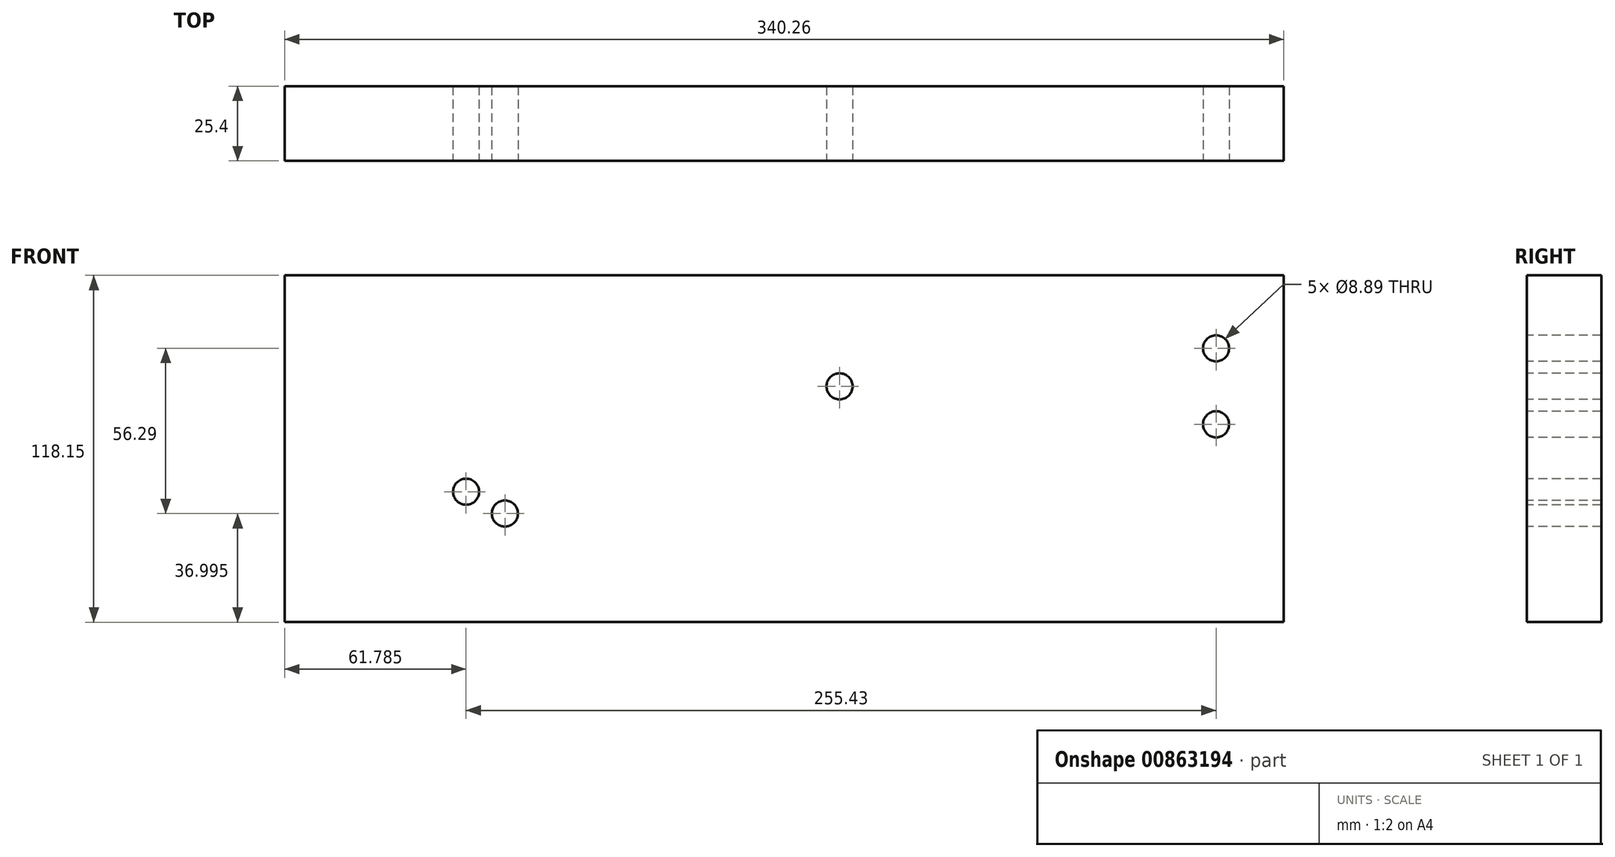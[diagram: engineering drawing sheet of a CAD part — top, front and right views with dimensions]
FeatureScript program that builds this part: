
annotation { "Feature Type Name" : "Feature", "Feature Type Description" : "" }
export const myFeature = defineFeature(function(context is Context, id is Id, definition is map)
    precondition{}
    {
        {
            var Q0;
            Q0=qCreatedBy(makeId("Front.planeOp"),FACE);
            var sketch = newSketch(context, id + "F0", { "sketchPlane" : qUnion([Q0])});
            skLineSegment(sketch, "E0.bottom", {"start": v(-97.64, 50.75) * mm, "end": v(242.62, 50.75) * mm});
            skLineSegment(sketch, "E0.top", {"start": v(-97.64, -67.4) * mm, "end": v(242.62, -67.4) * mm});
            skLineSegment(sketch, "E0.left", {"start": v(-97.64, 50.75) * mm, "end": v(-97.64, -67.4) * mm});
            skLineSegment(sketch, "E0.right", {"start": v(242.62, 50.75) * mm, "end": v(242.62, -67.4) * mm});
            skSolve(sketch);
        }
        {
            var Q0;
            Q0 = qSketchRegion(id + "F0", true);
            extrude(context, id + "F1", {"entities" : qUnion([Q0]), "depth" : 25.4 * mm, "offsetDistance" : 25.4 * mm});
        }
        {
            var Q0;
            Q0=makeQuery(id+"F1.opExtrude","CAP_FACE",FACE,{"disambiguationData":[OSD([sQuery(id+"F0.wireOp",EDGE,"E0.bottom"),sQuery(id+"F0.wireOp",EDGE,"E0.top"),sQuery(id+"F0.wireOp",EDGE,"E0.left"),sQuery(id+"F0.wireOp",EDGE,"E0.right")])],"isStart":false});
            var sketch = newSketch(context, id + "F2", { "sketchPlane" : qUnion([Q0])});
            skLineSegment(sketch, "E1.bottom", {"start": v(219.57, 0) * mm, "end": v(-36.92, 0) * mm});
            skLineSegment(sketch, "E1.top", {"start": v(219.57, 25.89) * mm, "end": v(-36.92, 25.89) * mm});
            skLineSegment(sketch, "E1.left", {"start": v(219.57, 0) * mm, "end": v(219.57, 25.89) * mm});
            skLineSegment(sketch, "E1.right", {"start": v(-36.92, 0) * mm, "end": v(-36.92, 25.89) * mm});
            skPoint(sketch, "E1.middle", {"position": v(91.33, 12.94) * mm});
            skLineSegment(sketch, "E2.bottom", {"start": v(-22.64, -30.4) * mm, "end": v(-49.07, -30.4) * mm, "construction": true});
            skLineSegment(sketch, "E2.top", {"start": v(-22.64, -15.54) * mm, "end": v(-49.07, -15.54) * mm, "construction": true});
            skLineSegment(sketch, "E2.left", {"start": v(-22.64, -30.4) * mm, "end": v(-22.64, -15.54) * mm, "construction": true});
            skLineSegment(sketch, "E2.right", {"start": v(-49.07, -30.4) * mm, "end": v(-49.07, -15.54) * mm, "construction": true});
            skPoint(sketch, "E2.middle", {"position": v(-35.86, -22.97) * mm});
            skSolve(sketch);
        }
        {
            var Q0;
            Q0=sQuery(id+"F2.wireOp",VERTEX,"E2.middle");
            var Q1;
            Q1=sQuery(id+"F2.wireOp",VERTEX,"E2.bottom.start");
            var Q2;
            Q2=sQuery(id+"F2.wireOp",VERTEX,"E1.bottom.start");
            var Q3;
            Q3=sQuery(id+"F2.wireOp",VERTEX,"E1.top.start");
            var Q4;
            Q4=sQuery(id+"F2.wireOp",VERTEX,"E1.middle");
            var Q5;
            Q5=makeQuery(id+"F1.opExtrude","SWEPT_BODY",BODY,{"disambiguationData":[OSD([sQuery(id+"F0.wireOp",EDGE,"E0.bottom"),sQuery(id+"F0.wireOp",EDGE,"E0.top"),sQuery(id+"F0.wireOp",EDGE,"E0.left"),sQuery(id+"F0.wireOp",EDGE,"E0.right")])]});
            hole(context, id + "F3", {"style" : HoleStyle.SIMPLE, "endStyle" : HoleEndStyle.THROUGH, "holeDiameter" : 8.9 * mm, "majorDiameter" : 6.35 * mm, "isTappedThrough" : true, "tappedDepth" : 12.7 * mm, "tapClearance" : 3, "locations" : qUnion([Q0, Q1, Q2, Q3, Q4]), "scope" : qUnion([Q5])});
        }
    });
